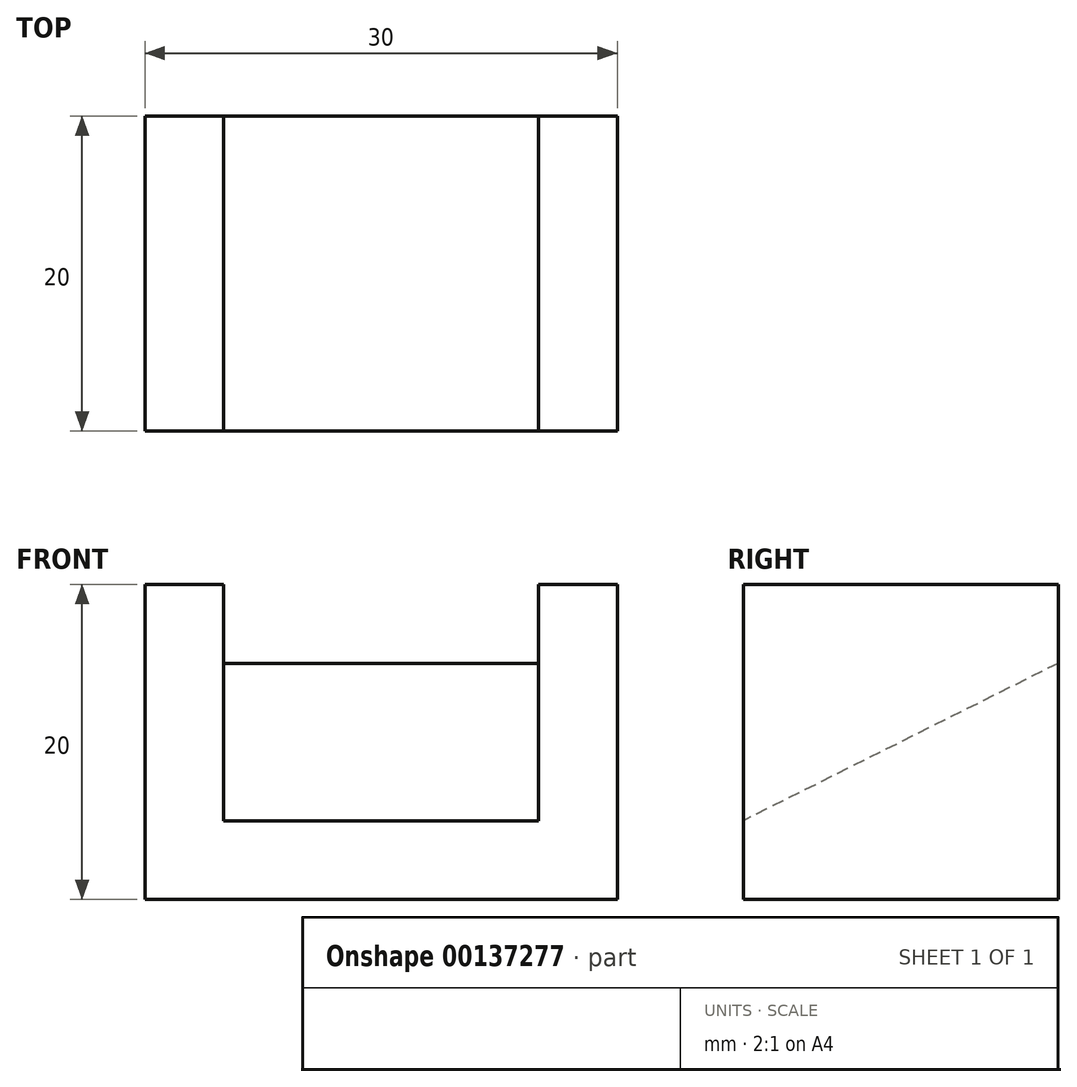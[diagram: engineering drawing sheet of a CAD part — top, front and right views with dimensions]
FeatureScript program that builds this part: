
annotation { "Feature Type Name" : "Feature", "Feature Type Description" : "" }
export const myFeature = defineFeature(function(context is Context, id is Id, definition is map)
    precondition{}
    {
        {
            var Q0;
            Q0=qCreatedBy(makeId("Front.planeOp"),FACE);
            var sketch = newSketch(context, id + "F0", { "sketchPlane" : qUnion([Q0])});
            skLineSegment(sketch, "E0.bottom", {"start": v(0, 0) * mm, "end": v(30, 0) * mm});
            skLineSegment(sketch, "E0.top", {"start": v(0, 20) * mm, "end": v(30, 20) * mm});
            skLineSegment(sketch, "E0.left", {"start": v(0, 0) * mm, "end": v(0, 20) * mm});
            skLineSegment(sketch, "E0.right", {"start": v(30, 0) * mm, "end": v(30, 20) * mm});
            skLineSegment(sketch, "E1", {"start": v(5, 20) * mm, "end": v(5, 0) * mm});
            skLineSegment(sketch, "E2", {"start": v(25, 20) * mm, "end": v(25, 0) * mm});
            skSolve(sketch);
        }
        {
            var Q0;
            Q0 = qSketchRegion(id + "F0", true);
            extrude(context, id + "F1", {"entities" : qUnion([Q0]), "depth" : 20 * mm});
        }
        {
            var Q0;
            Q0=makeQuery(id+"F1.opExtrude","SWEPT_FACE",FACE,{"disambiguationData":[OSD([sQuery(id+"F0.wireOp",EDGE,"E0.right")])]});
            var sketch = newSketch(context, id + "F2", { "sketchPlane" : qUnion([Q0])});
            skLineSegment(sketch, "E3", {"start": v(0, 20) * mm, "end": v(0, 15) * mm});
            skLineSegment(sketch, "E4", {"start": v(0, 15) * mm, "end": v(-20, 5) * mm});
            skLineSegment(sketch, "E5", {"start": v(-20, 5) * mm, "end": v(-20, 20) * mm});
            skLineSegment(sketch, "E6", {"start": v(-20, 20) * mm, "end": v(0, 20) * mm});
            skSolve(sketch);
        }
        {
            var Q0;
            Q0=makeQuery(id+"F2.imprint","IMPRINT",FACE,{"disambiguationData":[TD([[makeQuery(id+"F2.imprint","IMPRINT",EDGE,{"derivedFrom":sQuery(id+"F2.wireOp",EDGE,"E3")}),1.0]])]});
            extrude(context, id + "F3", {"entities" : qUnion([Q0]), "operationType" : NewBodyOperationType.REMOVE, "oppositeDirection" : true, "depth" : 25 * mm, "hasSecondDirection" : true, "secondDirectionOppositeDirection" : true, "secondDirectionDepth" : 5 * mm});
        }
    });
